# Revit family: Wicstyle77FP_Fixed_frame_EI30_T30
name_source: partatom
category: Doors
revit_build: Autodesk Revit Architecture 2014 (Build: 20130308_1515(x64)
units: mm (PartAtom-declared; Revit-internal decimal feet)

## types (1)
- Wicstyle77FP_Fixed_frame_EI30_T30
    Bottom Offset = 26 mm
    Clearance passage dimensions = Single-leaf 1,362 x 2,500 mm, Double-leaf 2,500 x 2,500 mm, Fixed glazing element height up to 3,500 mm, unlimited width
    Date of publishing = 3/14/2015
    Description = WICSTYLE 77FP provides 30 minutes’ fire resistance with profile elevations that are identical to a WICSTYLE 77 standard door, meaning that it ensures all the doors in your building have the same design. Consequently, this range fulfils the requirements of class EI30 and/or class T30/F30 for single and double-leaf doors with large leaf dimensions, without the need for fire protection inserts in this class.
    Design country = Germany
    Door Offset = 60 mm  [stored 0.19685 ft]
    Edition number = 1
    Filling thickness = 23 or 36 mm Type 30 pyrostop glass
    Filling weights = Up to 200 kg
    Fire protection class in accordance with DIN 4102 = T30-1 and T30-2, F30 glazing
    Fire protection class in accordance with DIN EN 13501-2 = EI30-1, EI30 glazing
    Frame 1020449 = Yes
    Frame 1021361 = No
    Frame Depth = 77 mm  [stored 0.252625 ft]
    Frame Material = WICONA - Aluminium - RAL7016 - Anthracite Grey - Matt
    Function = Interior
    Glass Material = WICONA -  Glass
    Glass Offset 1 = 49 mm
    Glass Offset 2 = 28 mm
    Handle Material = Aluminium
    Height = 2100 mm
    Leaf Material = WICONA - Aluminium - RAL7016 - Anthracite Grey - Matt
    MPlus_1021369 = No
    Manufacturer = Wicona
    Manufacturer country = Germany
    Manufacturer name = Wicona
    Material main = Aluminium
    Material secondary = Glass
    Model = Wicstyle 77FP
    Mullion 1021364 = Yes
    Mullion 1021365 = No
    Mullion 1021367 = No
    Mullion 1021369 = No
    Mullion Width 1 = 800 mm  [stored 2.62467 ft]
    Nominal height = 210000
    Nominal width = 140000
    Opening Line Lenght = 1502 mm
    Product Guid = 0a2d15cc-3e25-4d95-9584-ec63cf4c32b4
    Product SKU = WICSTYLE_77_FP_D
    Product data url = http://bimobject.com
    Product family = Windows & Doors
    Product group = Windows
    QR code = http://bimobject.com
    URL = http://www.wicona.com
http://www.wicona.com
    Wall Closure = By host
    Weight Net (Kg) = 0
    Width = 1600 mm

note: [stored X ft] marks values corroborated as IEEE doubles in the binary element streams (Revit-internal decimal feet)

## geometry (parser evidence)
native form markers: Blend x4, Sweep x6
no freeform markers — native parametric forms only
